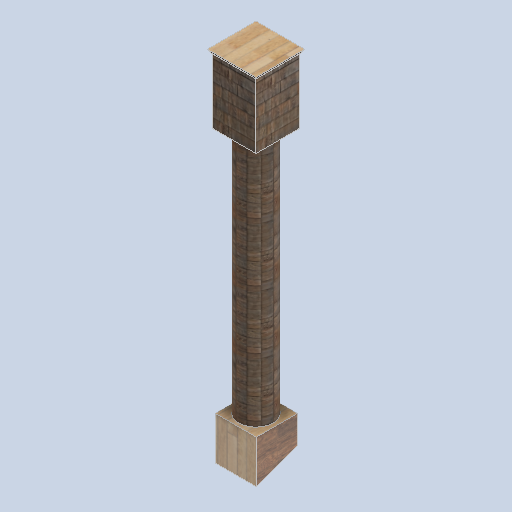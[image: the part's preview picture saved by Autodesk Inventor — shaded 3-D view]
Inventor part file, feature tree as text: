
AUTODESK INVENTOR PART (.ipt)
format: ipt  version: 2024.2 (Build 282272000, 272)  size: 174,080 bytes
history: native  units: in
note: dims shown in document units (in); Inventor stores cm internally (conversion verified against a paired STEP export)
features: sketch x5, other x3, plane x1
ambient origin geometry x8: Origin, YZ Plane, XZ Plane, XY Plane, X Axis, Y Axis, Z Axis, Center Point
bodies: Solid1 (feature_tree)
feature tree (9):
  other  "side_pillar_01.ipt"
  other  "Solid1::side_pillar_01.ipt"
  other  "TaggingFeature1"
  sketch  "Sketch1"  dims[d0=0.3937in]
  sketch  "Sketch2"
  sketch  "Sketch3"
  sketch  "Sketch4"
  sketch  "Sketch5"
  plane  "Work Plane3"
